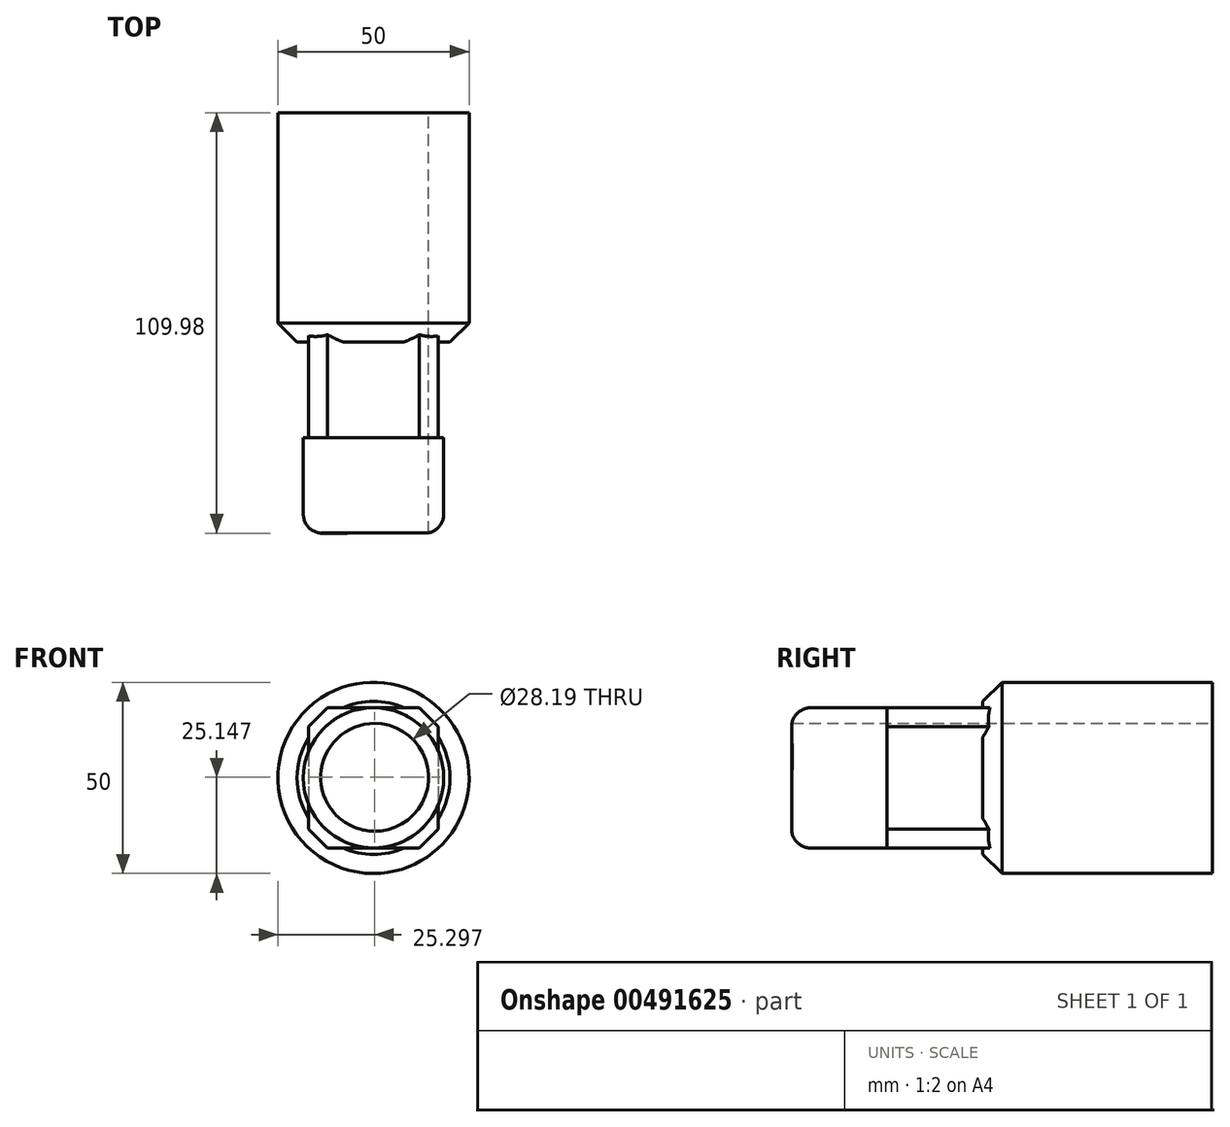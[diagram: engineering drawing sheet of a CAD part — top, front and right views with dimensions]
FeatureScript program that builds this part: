
annotation { "Feature Type Name" : "Feature", "Feature Type Description" : "" }
export const myFeature = defineFeature(function(context is Context, id is Id, definition is map)
    precondition{}
    {
        {
            var Q0;
            Q0=qCreatedBy(makeId("Front.planeOp"),FACE);
            var sketch = newSketch(context, id + "F0", { "sketchPlane" : qUnion([Q0])});
            skCircle(sketch, "E0", {"center": v(0, 0) * mm, "radius": 25 * mm});
            skSolve(sketch);
        }
        {
            var Q0;
            Q0 = qSketchRegion(id + "F0", true);
            extrude(context, id + "F1", {"entities" : qUnion([Q0]), "depth" : 60 * mm});
        }
        {
            var Q0;
            Q0=makeQuery(id+"F1.opExtrude","CAP_FACE",FACE,{"disambiguationData":[OSD([sQuery(id+"F0.wireOp",EDGE,"E0")])],"isStart":false});
            var sketch = newSketch(context, id + "F2", { "sketchPlane" : qUnion([Q0])});
            skLineSegment(sketch, "E1.bottom", {"start": v(16.98, 18.35) * mm, "end": v(-16.98, 18.35) * mm});
            skLineSegment(sketch, "E1.top", {"start": v(16.98, -18.35) * mm, "end": v(-16.98, -18.35) * mm});
            skLineSegment(sketch, "E1.left", {"start": v(16.98, 18.35) * mm, "end": v(16.98, -18.35) * mm});
            skLineSegment(sketch, "E1.right", {"start": v(-16.98, 18.35) * mm, "end": v(-16.98, -18.35) * mm});
            skPoint(sketch, "E1.middle", {"position": v(0, 0) * mm});
            skSolve(sketch);
        }
        {
            var Q0;
            Q0 = qSketchRegion(id + "F2", true);
            extrude(context, id + "F3", {"entities" : qUnion([Q0]), "operationType" : NewBodyOperationType.ADD, "depth" : 25 * mm});
        }
        {
            var Q0;
            Q0=makeQuery(id+"F3.opExtrude","CAP_FACE",FACE,{"disambiguationData":[OSD([sQuery(id+"F2.wireOp",EDGE,"E1.bottom"),sQuery(id+"F2.wireOp",EDGE,"E1.top"),sQuery(id+"F2.wireOp",EDGE,"E1.left"),sQuery(id+"F2.wireOp",EDGE,"E1.right")])],"isStart":false});
            var sketch = newSketch(context, id + "F4", { "sketchPlane" : qUnion([Q0])});
            skCircle(sketch, "E2", {"center": v(0, 0) * mm, "radius": 18.35 * mm});
            skSolve(sketch);
        }
        {
            var Q0;
            Q0 = qSketchRegion(id + "F4", true);
            extrude(context, id + "F5", {"entities" : qUnion([Q0]), "operationType" : NewBodyOperationType.ADD, "depth" : 25 * mm});
        }
        {
            var Q0;
            Q0=makeQuery(id+"F5.opExtrude","CAP_EDGE",EDGE,{"disambiguationData":[OSD([sQuery(id+"F4.wireOp",EDGE,"E2")])],"isStart":false});
            fillet(context, id + "F6", {"entities" : qUnion([Q0]), "radius" : 5 * mm, "tangentPropagation" : true, "allowEdgeOverflow" : false});
        }
        {
            var Q0;
            Q0=makeQuery(id+"F3.opExtrude","SWEPT_EDGE",EDGE,{"disambiguationData":[OSD([sQuery(id+"F0.wireOp",EDGE,"E0"),sQuery(id+"F2.wireOp",EDGE,"E1.bottom"),sQuery(id+"F2.wireOp",EDGE,"E1.right")])]});
            var Q1;
            Q1=makeQuery(id+"F3.opExtrude","SWEPT_EDGE",EDGE,{"disambiguationData":[OSD([sQuery(id+"F0.wireOp",EDGE,"E0"),sQuery(id+"F2.wireOp",EDGE,"E1.bottom"),sQuery(id+"F2.wireOp",EDGE,"E1.left")])]});
            var Q2;
            Q2=makeQuery(id+"F3.opExtrude","SWEPT_EDGE",EDGE,{"disambiguationData":[OSD([sQuery(id+"F0.wireOp",EDGE,"E0"),sQuery(id+"F2.wireOp",EDGE,"E1.top"),sQuery(id+"F2.wireOp",EDGE,"E1.left")])]});
            var Q3;
            Q3=makeQuery(id+"F3.opExtrude","SWEPT_EDGE",EDGE,{"disambiguationData":[OSD([sQuery(id+"F0.wireOp",EDGE,"E0"),sQuery(id+"F2.wireOp",EDGE,"E1.top"),sQuery(id+"F2.wireOp",EDGE,"E1.right")])]});
            chamfer(context, id + "F7", {"entities" : qUnion([Q0, Q1, Q2, Q3]), "width" : 5 * mm, "tangentPropagation" : true});
        }
        {
            var Q0;
            {var subQ0=sQuery(id+"F0.wireOp",EDGE,"E0");Q0=makeQuery(id+"F3.boolean.opBoolean","SPLIT",EDGE,{"disambiguationData":[TD([makeQuery(id+"F1.opExtrude","SWEPT_FACE",FACE,{"disambiguationData":[OSD([subQ0])]}),makeQuery(id+"F1.opExtrude","CAP_FACE",FACE,{"disambiguationData":[OSD([subQ0])],"isStart":false}),makeQuery(id+"F3.opExtrude","SWEPT_FACE",FACE,{"disambiguationData":[OSD([sQuery(id+"F2.wireOp",EDGE,"E1.bottom")])]}),makeQuery(id+"F3.opExtrude","SWEPT_FACE",FACE,{"disambiguationData":[OSD([sQuery(id+"F2.wireOp",EDGE,"E1.top")])]}),makeQuery(id+"F3.opExtrude","SWEPT_FACE",FACE,{"disambiguationData":[OSD([sQuery(id+"F2.wireOp",EDGE,"E1.left")])]})])],"derivedFrom":makeQuery(id+"F1.opExtrude","CAP_EDGE",EDGE,{"disambiguationData":[OSD([subQ0])],"isStart":false})});}
            chamfer(context, id + "F8", {"entities" : qUnion([Q0]), "width" : 5 * mm, "tangentPropagation" : true});
        }
        {
            var Q0;
            Q0=makeQuery(id+"F1.opExtrude","CAP_FACE",FACE,{"disambiguationData":[OSD([sQuery(id+"F0.wireOp",EDGE,"E0")])],"isStart":true});
            var sketch = newSketch(context, id + "F9", { "sketchPlane" : qUnion([Q0])});
            skCircle(sketch, "E3", {"center": v(-0.3, 0.15) * mm, "radius": 14.1 * mm});
            skSolve(sketch);
        }
        {
            var Q0;
            Q0 = qSketchRegion(id + "F9", true);
            extrude(context, id + "F10", {"entities" : qUnion([Q0]), "operationType" : NewBodyOperationType.REMOVE, "oppositeDirection" : true, "depth" : 200 * mm});
        }
    });
